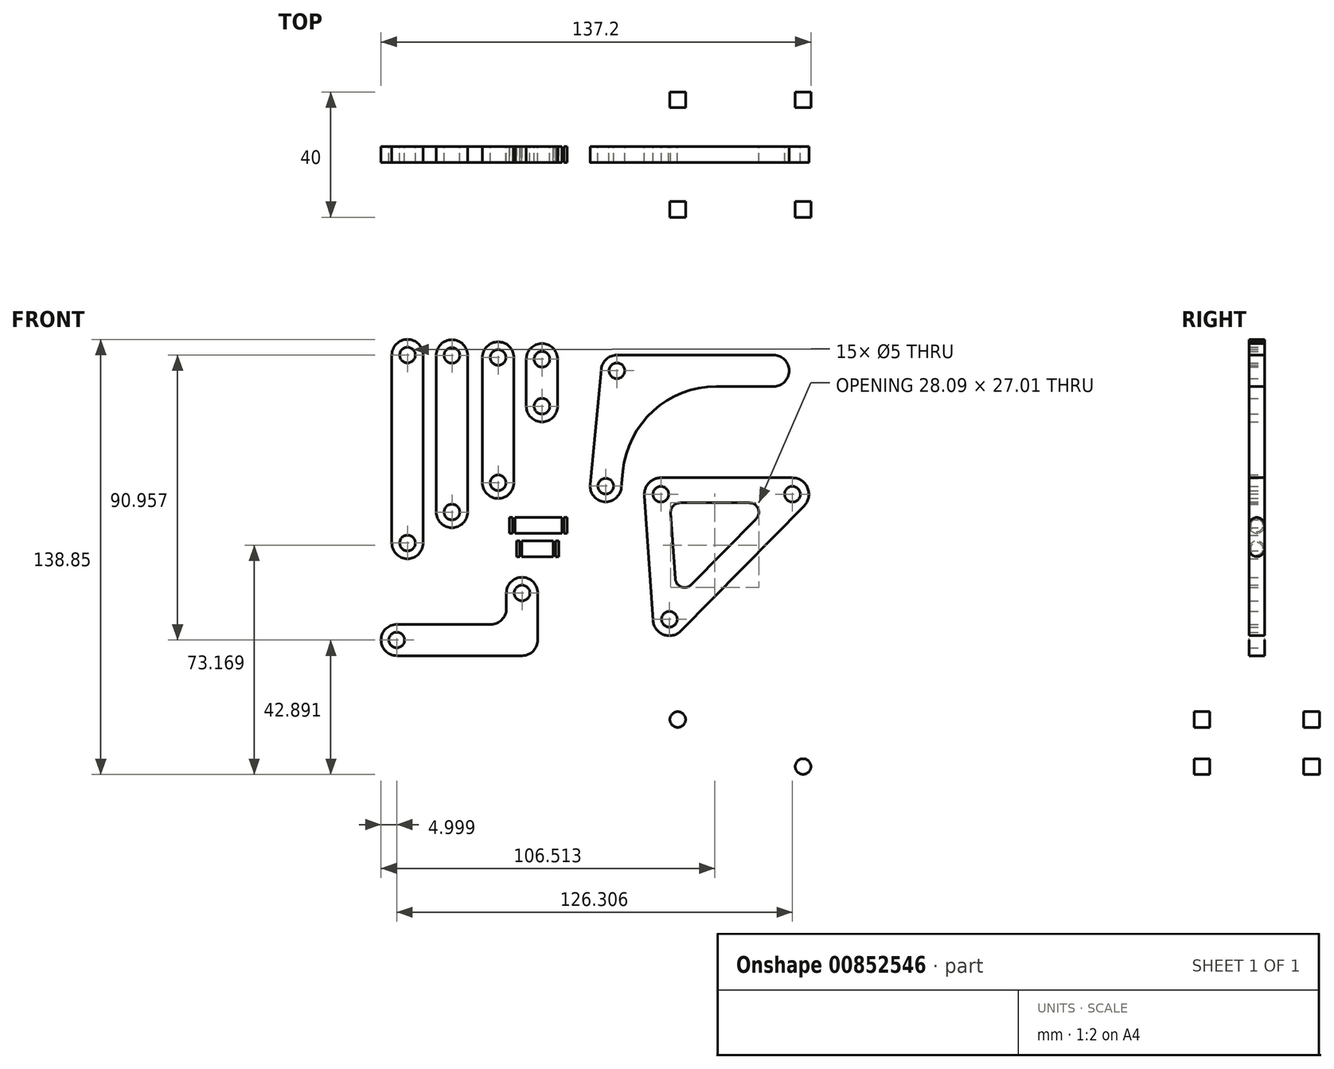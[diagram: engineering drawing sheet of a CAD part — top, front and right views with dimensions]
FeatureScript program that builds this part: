
annotation { "Feature Type Name" : "Feature", "Feature Type Description" : "" }
export const myFeature = defineFeature(function(context is Context, id is Id, definition is map)
    precondition{}
    {
        {
            assignVariable(context, id + "F0", {"name" : "T", "anyValue" : 5});
        }
        {
            assignVariable(context, id + "F1", {"name" : "W", "anyValue" : 40});
        }
        {
            var Q0;
            Q0=qCreatedBy(makeId("Front.planeOp"),FACE);
            var sketch = newSketch(context, id + "F2", { "sketchPlane" : qUnion([Q0])});
            skLineSegment(sketch, "E0", {"start": v(-8.35, 51.22) * mm, "end": v(-8.35, 66.22) * mm});
            skLineSegment(sketch, "E1", {"start": v(-18.35, 51.22) * mm, "end": v(-18.35, 66.22) * mm});
            skArc(sketch, "E2", {"start": v(-8.35, 66.22) * mm, "mid": v(-13.35, 71.22) * mm, "end": v(-18.35, 66.22) * mm});
            skArc(sketch, "E3", {"start": v(-18.35, 51.22) * mm, "mid": v(-13.35, 46.22) * mm, "end": v(-8.35, 51.22) * mm});
            skCircle(sketch, "E4", {"center": v(-13.35, 66.22) * mm, "radius": 2.5 * mm});
            skCircle(sketch, "E5", {"center": v(-13.35, 51.22) * mm, "radius": 2.5 * mm});
            skSolve(sketch);
        }
        {
            var Q0;
            Q0 = qSketchRegion(id + "F2", true);
            extrude(context, id + "F3", {"entities" : qUnion([Q0]), "endBound" : BoundingType.SYMMETRIC, "depth" : (getVariable(context, 'T')) * mm, "offsetDistance" : 25 * mm});
        }
        {
            var Q0;
            Q0=qCreatedBy(makeId("Front.planeOp"),FACE);
            var sketch = newSketch(context, id + "F4", { "sketchPlane" : qUnion([Q0])});
            skLineSegment(sketch, "E6", {"start": v(-32.34, 66.78) * mm, "end": v(-32.34, 26.78) * mm});
            skLineSegment(sketch, "E7", {"start": v(-22.34, 26.78) * mm, "end": v(-22.34, 66.78) * mm});
            skArc(sketch, "E8", {"start": v(-22.34, 66.78) * mm, "mid": v(-27.34, 71.78) * mm, "end": v(-32.34, 66.78) * mm});
            skArc(sketch, "E9", {"start": v(-32.34, 26.78) * mm, "mid": v(-27.34, 21.78) * mm, "end": v(-22.34, 26.78) * mm});
            skCircle(sketch, "E10", {"center": v(-27.34, 26.78) * mm, "radius": 2.5 * mm});
            skCircle(sketch, "E11", {"center": v(-27.34, 66.78) * mm, "radius": 2.5 * mm});
            skSolve(sketch);
        }
        {
            var Q0;
            Q0 = qSketchRegion(id + "F4", true);
            extrude(context, id + "F5", {"entities" : qUnion([Q0]), "endBound" : BoundingType.SYMMETRIC, "depth" : (getVariable(context, 'T')) * mm, "offsetDistance" : 25 * mm});
        }
        {
            var Q0;
            Q0=qCreatedBy(makeId("Front.planeOp"),FACE);
            var sketch = newSketch(context, id + "F6", { "sketchPlane" : qUnion([Q0])});
            skLineSegment(sketch, "E12", {"start": v(-47.08, 67.45) * mm, "end": v(-47.08, 17.45) * mm});
            skLineSegment(sketch, "E13", {"start": v(-37.08, 67.45) * mm, "end": v(-37.08, 17.45) * mm});
            skArc(sketch, "E14", {"start": v(-47.08, 17.45) * mm, "mid": v(-42.08, 12.45) * mm, "end": v(-37.08, 17.45) * mm});
            skArc(sketch, "E15", {"start": v(-37.08, 67.45) * mm, "mid": v(-42.08, 72.45) * mm, "end": v(-47.08, 67.45) * mm});
            skCircle(sketch, "E16", {"center": v(-42.08, 67.45) * mm, "radius": 2.5 * mm});
            skCircle(sketch, "E17", {"center": v(-42.08, 17.45) * mm, "radius": 2.5 * mm});
            skSolve(sketch);
        }
        {
            var Q0;
            Q0 = qSketchRegion(id + "F6", true);
            extrude(context, id + "F7", {"entities" : qUnion([Q0]), "endBound" : BoundingType.SYMMETRIC, "depth" : (getVariable(context, 'T')) * mm, "offsetDistance" : 25 * mm});
        }
        {
            var Q0;
            Q0=qCreatedBy(makeId("Front.planeOp"),FACE);
            var sketch = newSketch(context, id + "F8", { "sketchPlane" : qUnion([Q0])});
            skLineSegment(sketch, "E18", {"start": v(-61.26, 67.56) * mm, "end": v(-61.26, 7.56) * mm});
            skLineSegment(sketch, "E19", {"start": v(-51.26, 7.56) * mm, "end": v(-51.26, 67.56) * mm});
            skArc(sketch, "E20", {"start": v(-51.26, 67.56) * mm, "mid": v(-56.26, 72.56) * mm, "end": v(-61.26, 67.56) * mm});
            skArc(sketch, "E21", {"start": v(-61.26, 7.56) * mm, "mid": v(-56.26, 2.56) * mm, "end": v(-51.26, 7.56) * mm});
            skCircle(sketch, "E22", {"center": v(-56.26, 67.56) * mm, "radius": 2.5 * mm});
            skCircle(sketch, "E23", {"center": v(-56.26, 7.56) * mm, "radius": 2.5 * mm});
            skSolve(sketch);
        }
        {
            var Q0;
            Q0 = qSketchRegion(id + "F8", true);
            extrude(context, id + "F9", {"entities" : qUnion([Q0]), "endBound" : BoundingType.SYMMETRIC, "depth" : (getVariable(context, 'T')) * mm, "offsetDistance" : 25 * mm});
        }
        {
            var Q0;
            Q0=qCreatedBy(makeId("Front.planeOp"),FACE);
            var sketch = newSketch(context, id + "F10", { "sketchPlane" : qUnion([Q0])});
            skLineSegment(sketch, "E24", {"start": v(60.57, 67.55) * mm, "end": v(10.57, 67.55) * mm});
            skLineSegment(sketch, "E25", {"start": v(5.6, 63.03) * mm, "end": v(2.04, 26.2) * mm});
            skLineSegment(sketch, "E26", {"start": v(12, 25.24) * mm, "end": v(12.5, 30.44) * mm});
            skLineSegment(sketch, "E27", {"start": v(42.35, 57.55) * mm, "end": v(60.57, 57.55) * mm});
            skArc(sketch, "E28", {"start": v(2.04, 26.2) * mm, "mid": v(6.53, 20.74) * mm, "end": v(12, 25.24) * mm});
            skArc(sketch, "E29", {"start": v(10.57, 67.55) * mm, "mid": v(7.21, 66.25) * mm, "end": v(5.6, 63.03) * mm});
            skArc(sketch, "E30", {"start": v(60.57, 57.55) * mm, "mid": v(65.57, 62.55) * mm, "end": v(60.57, 67.55) * mm});
            skArc(sketch, "E31", {"start": v(42.35, 57.55) * mm, "mid": v(22.19, 49.76) * mm, "end": v(12.5, 30.44) * mm});
            skCircle(sketch, "E32", {"center": v(7.01, 25.72) * mm, "radius": 2.5 * mm});
            skCircle(sketch, "E33", {"center": v(10.57, 62.55) * mm, "radius": 2.5 * mm});
            skSolve(sketch);
        }
        {
            var Q0;
            Q0=makeQuery(id+"F10.imprint","IMPRINT",FACE,{"disambiguationData":[TD([[makeQuery(id+"F10.imprint","IMPRINT",EDGE,{"derivedFrom":sQuery(id+"F10.wireOp",EDGE,"E24")}),1.0]])]});
            extrude(context, id + "F11", {"entities" : qUnion([Q0]), "endBound" : BoundingType.SYMMETRIC, "depth" : (getVariable(context, 'T')) * mm, "offsetDistance" : 25 * mm});
        }
        {
            var Q0;
            Q0=qCreatedBy(makeId("Front.planeOp"),FACE);
            var sketch = newSketch(context, id + "F12", { "sketchPlane" : qUnion([Q0])});
            skLineSegment(sketch, "E34", {"start": v(19.37, 22.78) * mm, "end": v(22.08, -17.13) * mm});
            skLineSegment(sketch, "E35", {"start": v(31.06, -20.46) * mm, "end": v(70.35, 19.45) * mm});
            skLineSegment(sketch, "E36", {"start": v(66.6, 28.38) * mm, "end": v(24.6, 28.38) * mm});
            skArc(sketch, "E37", {"start": v(24.6, 28.38) * mm, "mid": v(20.77, 26.72) * mm, "end": v(19.37, 22.78) * mm});
            skArc(sketch, "E38", {"start": v(22.08, -17.13) * mm, "mid": v(25.5, -21.7) * mm, "end": v(31.06, -20.46) * mm});
            skArc(sketch, "E39", {"start": v(70.35, 19.45) * mm, "mid": v(71.45, 25.16) * mm, "end": v(66.6, 28.38) * mm});
            skCircle(sketch, "E40", {"center": v(24.6, 23.13) * mm, "radius": 2.5 * mm});
            skCircle(sketch, "E41", {"center": v(27.32, -16.77) * mm, "radius": 2.5 * mm});
            skCircle(sketch, "E42", {"center": v(66.6, 23.13) * mm, "radius": 2.5 * mm});
            skLineSegment(sketch, "E43", {"start": v(30.76, 20.38) * mm, "end": v(52.88, 20.38) * mm});
            skLineSegment(sketch, "E44", {"start": v(55.01, 15.28) * mm, "end": v(34.33, -5.74) * mm});
            skLineSegment(sketch, "E45", {"start": v(27.77, 17.18) * mm, "end": v(29.2, -3.83) * mm});
            skArc(sketch, "E46", {"start": v(29.2, -3.83) * mm, "mid": v(31.15, -6.44) * mm, "end": v(34.33, -5.74) * mm});
            skArc(sketch, "E47", {"start": v(30.76, 20.38) * mm, "mid": v(28.57, 19.43) * mm, "end": v(27.77, 17.18) * mm});
            skArc(sketch, "E48", {"start": v(55.01, 15.28) * mm, "mid": v(55.64, 18.54) * mm, "end": v(52.88, 20.38) * mm});
            skLineSegment(sketch, "E49", {"start": v(52.88, 28.38) * mm, "end": v(52.88, 20.38) * mm, "construction": true});
            skLineSegment(sketch, "E50", {"start": v(60.71, 9.67) * mm, "end": v(55.01, 15.28) * mm, "construction": true});
            skLineSegment(sketch, "E51", {"start": v(19.78, 16.64) * mm, "end": v(27.77, 17.18) * mm, "construction": true});
            skSolve(sketch);
        }
        {
            var Q0;
            Q0 = qSketchRegion(id + "F12", true);
            extrude(context, id + "F13", {"entities" : qUnion([Q0]), "endBound" : BoundingType.SYMMETRIC, "depth" : (getVariable(context, 'T')) * mm, "offsetDistance" : 25 * mm});
        }
        {
            var Q0;
            Q0=qCreatedBy(makeId("Front.planeOp"),FACE);
            var sketch = newSketch(context, id + "F14", { "sketchPlane" : qUnion([Q0])});
            skLineSegment(sketch, "E52", {"start": v(-21.44, 5.72) * mm, "end": v(-21.44, 8.22) * mm});
            skLineSegment(sketch, "E53", {"start": v(-21.44, 8.22) * mm, "end": v(-20.44, 8.22) * mm});
            skLineSegment(sketch, "E54", {"start": v(-20.44, 8.22) * mm, "end": v(-20.44, 7.72) * mm});
            skLineSegment(sketch, "E55", {"start": v(-20.44, 7.72) * mm, "end": v(-19.74, 7.72) * mm});
            skLineSegment(sketch, "E56", {"start": v(-19.74, 7.72) * mm, "end": v(-19.74, 8.22) * mm});
            skLineSegment(sketch, "E57", {"start": v(-19.74, 8.22) * mm, "end": v(-9.74, 8.22) * mm});
            skLineSegment(sketch, "E58", {"start": v(-9.74, 8.22) * mm, "end": v(-9.74, 7.72) * mm});
            skLineSegment(sketch, "E59", {"start": v(-9.74, 7.72) * mm, "end": v(-9.04, 7.72) * mm});
            skLineSegment(sketch, "E60", {"start": v(-9.04, 7.72) * mm, "end": v(-9.04, 8.22) * mm});
            skLineSegment(sketch, "E61", {"start": v(-9.04, 8.22) * mm, "end": v(-8.04, 8.22) * mm});
            skLineSegment(sketch, "E62", {"start": v(-8.04, 8.22) * mm, "end": v(-8.04, 5.72) * mm});
            skLineSegment(sketch, "E63", {"start": v(-8.04, 5.72) * mm, "end": v(-21.44, 5.72) * mm});
            skSolve(sketch);
        }
        {
            var Q0;
            Q0=makeQuery(id+"F14.imprint","IMPRINT",FACE,{"disambiguationData":[TD([[makeQuery(id+"F14.imprint","IMPRINT",EDGE,{"derivedFrom":sQuery(id+"F14.wireOp",EDGE,"E52")}),-1.0]])]});
            var Q1;
            Q1=sQuery(id+"F14.wireOp",EDGE,"E63");
            revolve(context, id + "F15", {"surfaceOperationType" : NewSurfaceOperationType.NEW, "entities" : qUnion([Q0]), "axis" : qUnion([Q1]), "revolveType" : RevolveType.FULL});
        }
        {
            var Q0;
            Q0=qCreatedBy(makeId("Front.planeOp"),FACE);
            var sketch = newSketch(context, id + "F16", { "sketchPlane" : qUnion([Q0])});
            skLineSegment(sketch, "E64", {"start": v(-23.7, 15.7) * mm, "end": v(-23.7, 13.2) * mm});
            skLineSegment(sketch, "E65", {"start": v(-23.7, 13.2) * mm, "end": v(-5.3, 13.2) * mm});
            skLineSegment(sketch, "E66", {"start": v(-5.3, 13.2) * mm, "end": v(-5.3, 15.7) * mm});
            skLineSegment(sketch, "E67", {"start": v(-5.3, 15.7) * mm, "end": v(-6.3, 15.7) * mm});
            skLineSegment(sketch, "E68", {"start": v(-6.3, 15.7) * mm, "end": v(-6.3, 15.2) * mm});
            skLineSegment(sketch, "E69", {"start": v(-6.3, 15.2) * mm, "end": v(-7, 15.2) * mm});
            skLineSegment(sketch, "E70", {"start": v(-7, 15.2) * mm, "end": v(-7, 15.7) * mm});
            skLineSegment(sketch, "E71", {"start": v(-7, 15.7) * mm, "end": v(-22, 15.7) * mm});
            skLineSegment(sketch, "E72", {"start": v(-22, 15.7) * mm, "end": v(-22, 15.2) * mm});
            skLineSegment(sketch, "E73", {"start": v(-22, 15.2) * mm, "end": v(-22.7, 15.2) * mm});
            skLineSegment(sketch, "E74", {"start": v(-22.7, 15.2) * mm, "end": v(-22.7, 15.7) * mm});
            skLineSegment(sketch, "E75", {"start": v(-22.7, 15.7) * mm, "end": v(-23.7, 15.7) * mm});
            skSolve(sketch);
        }
        {
            var Q0;
            Q0 = qSketchRegion(id + "F16", true);
            var Q1;
            Q1=sQuery(id+"F16.wireOp",EDGE,"E65");
            revolve(context, id + "F17", {"surfaceOperationType" : NewSurfaceOperationType.NEW, "entities" : qUnion([Q0]), "axis" : qUnion([Q1]), "revolveType" : RevolveType.FULL});
        }
        {
            var Q0;
            Q0=qCreatedBy(makeId("Front.planeOp"),FACE);
            var sketch = newSketch(context, id + "F18", { "sketchPlane" : qUnion([Q0])});
            skLineSegment(sketch, "E76", {"start": v(-59.7, -18.4) * mm, "end": v(-29.7, -18.4) * mm});
            skLineSegment(sketch, "E77", {"start": v(-24.7, -13.4) * mm, "end": v(-24.7, -8.4) * mm});
            skLineSegment(sketch, "E78", {"start": v(-14.7, -8.4) * mm, "end": v(-14.7, -23.4) * mm});
            skLineSegment(sketch, "E79", {"start": v(-19.7, -28.4) * mm, "end": v(-59.7, -28.4) * mm});
            skArc(sketch, "E80", {"start": v(-59.7, -18.4) * mm, "mid": v(-64.7, -23.4) * mm, "end": v(-59.7, -28.4) * mm});
            skArc(sketch, "E81", {"start": v(-14.7, -8.4) * mm, "mid": v(-19.7, -3.4) * mm, "end": v(-24.7, -8.4) * mm});
            skPoint(sketch, "E82.visualSharp", {"position": v(-24.7, -18.4) * mm});
            skArc(sketch, "E82.filletArc", {"start": v(-29.7, -18.4) * mm, "mid": v(-26.17, -16.93) * mm, "end": v(-24.7, -13.4) * mm});
            skPoint(sketch, "E83.visualSharp", {"position": v(-14.7, -28.4) * mm});
            skArc(sketch, "E83.filletArc", {"start": v(-19.7, -28.4) * mm, "mid": v(-16.17, -26.93) * mm, "end": v(-14.7, -23.4) * mm});
            skCircle(sketch, "E84", {"center": v(-59.7, -23.4) * mm, "radius": 2.5 * mm});
            skCircle(sketch, "E85", {"center": v(-19.7, -8.4) * mm, "radius": 2.5 * mm});
            skSolve(sketch);
        }
        {
            var Q0;
            Q0 = qSketchRegion(id + "F18", true);
            extrude(context, id + "F19", {"entities" : qUnion([Q0]), "endBound" : BoundingType.SYMMETRIC, "depth" : (getVariable(context, 'T')) * mm, "offsetDistance" : 25 * mm});
        }
        {
            var Q0;
            Q0=qCreatedBy(makeId("Front.planeOp"),FACE);
            var sketch = newSketch(context, id + "F20", { "sketchPlane" : qUnion([Q0])});
            skLineSegment(sketch, "E86.bottom", {"start": v(-80, -39.79) * mm, "end": v(80, -39.79) * mm});
            skLineSegment(sketch, "E86.top", {"start": v(-80, -69.79) * mm, "end": v(80, -69.79) * mm});
            skLineSegment(sketch, "E86.left", {"start": v(-80, -39.79) * mm, "end": v(-80, -69.79) * mm});
            skLineSegment(sketch, "E86.right", {"start": v(80, -39.79) * mm, "end": v(80, -69.79) * mm});
            skSolve(sketch);
        }
        {
            var Q0;
            Q0=makeQuery(id+"F20.imprint","IMPRINT",FACE,{"disambiguationData":[TD([[makeQuery(id+"F20.imprint","IMPRINT",EDGE,{"derivedFrom":sQuery(id+"F20.wireOp",EDGE,"E86.bottom")}),-1.0]])]});
            extrude(context, id + "F21", {"entities" : qUnion([Q0]), "endBound" : BoundingType.SYMMETRIC, "depth" : (getVariable(context, 'W')) * mm, "offsetDistance" : 25 * mm});
        }
        {
            var Q0;
            Q0=makeQuery(id+"F21.opExtrude","SWEPT_FACE",FACE,{"disambiguationData":[OSD([sQuery(id+"F20.wireOp",EDGE,"E86.bottom")])]});
            var Q1;
            Q1=makeQuery(id+"F21.opExtrude","SWEPT_FACE",FACE,{"disambiguationData":[OSD([sQuery(id+"F20.wireOp",EDGE,"E86.top")])]});
            shell(context, id + "F22", {"entities" : qUnion([Q0, Q1]), "thickness" : (getVariable(context, 'T')) * mm});
        }
        {
            var Q0;
            Q0=makeQuery(id+"F21.opExtrude","CAP_FACE",FACE,{"disambiguationData":[OSD([sQuery(id+"F20.wireOp",EDGE,"E86.bottom"),sQuery(id+"F20.wireOp",EDGE,"E86.top"),sQuery(id+"F20.wireOp",EDGE,"E86.left"),sQuery(id+"F20.wireOp",EDGE,"E86.right")])],"isStart":false});
            var sketch = newSketch(context, id + "F23", { "sketchPlane" : qUnion([Q0])});
            skCircle(sketch, "E87", {"center": v(-70, -63.79) * mm, "radius": 2.5 * mm});
            skCircle(sketch, "E88", {"center": v(-30, -48.79) * mm, "radius": 2.5 * mm});
            skLineSegment(sketch, "E89", {"start": v(-70, -63.79) * mm, "end": v(-30, -63.79) * mm, "construction": true});
            skLineSegment(sketch, "E90", {"start": v(-30, -63.79) * mm, "end": v(-30, -48.79) * mm, "construction": true});
            skCircle(sketch, "E91.MirrorC", {"center": v(30, -48.79) * mm, "radius": 2.5 * mm});
            skCircle(sketch, "E92.MirrorC", {"center": v(70, -63.79) * mm, "radius": 2.5 * mm});
            skSolve(sketch);
        }
        {
            var Q0;
            Q0=makeQuery(id+"F23.imprint","IMPRINT",FACE,{"disambiguationData":[TD([[makeQuery(id+"F23.imprint","IMPRINT",EDGE,{"derivedFrom":sQuery(id+"F23.wireOp",EDGE,"E87")}),1.0]])]});
            var Q1;
            Q1=makeQuery(id+"F23.imprint","IMPRINT",FACE,{"disambiguationData":[TD([[makeQuery(id+"F23.imprint","IMPRINT",EDGE,{"derivedFrom":sQuery(id+"F23.wireOp",EDGE,"E88")}),1.0]])]});
            var Q2;
            Q2=makeQuery(id+"F23.imprint","IMPRINT",FACE,{"disambiguationData":[TD([[makeQuery(id+"F23.imprint","IMPRINT",EDGE,{"derivedFrom":sQuery(id+"F23.wireOp",EDGE,"E91.MirrorC")}),-1.0]])]});
            var Q3;
            Q3=makeQuery(id+"F23.imprint","IMPRINT",FACE,{"disambiguationData":[TD([[makeQuery(id+"F23.imprint","IMPRINT",EDGE,{"derivedFrom":sQuery(id+"F23.wireOp",EDGE,"E92.MirrorC")}),-1.0]])]});
            var Q4;
            Q4=makeQuery(id+"F21.opExtrude","CAP_FACE",FACE,{"disambiguationData":[OSD([sQuery(id+"F20.wireOp",EDGE,"E86.bottom"),sQuery(id+"F20.wireOp",EDGE,"E86.top"),sQuery(id+"F20.wireOp",EDGE,"E86.left"),sQuery(id+"F20.wireOp",EDGE,"E86.right")])],"isStart":true});
            extrude(context, id + "F24", {"entities" : qUnion([Q0, Q1, Q2, Q3]), "operationType" : NewBodyOperationType.REMOVE, "endBound" : BoundingType.UP_TO_SURFACE, "oppositeDirection" : true, "depth" : 25 * mm, "endBoundEntityFace" : qUnion([Q4]), "offsetDistance" : 25 * mm});
        }
    });
